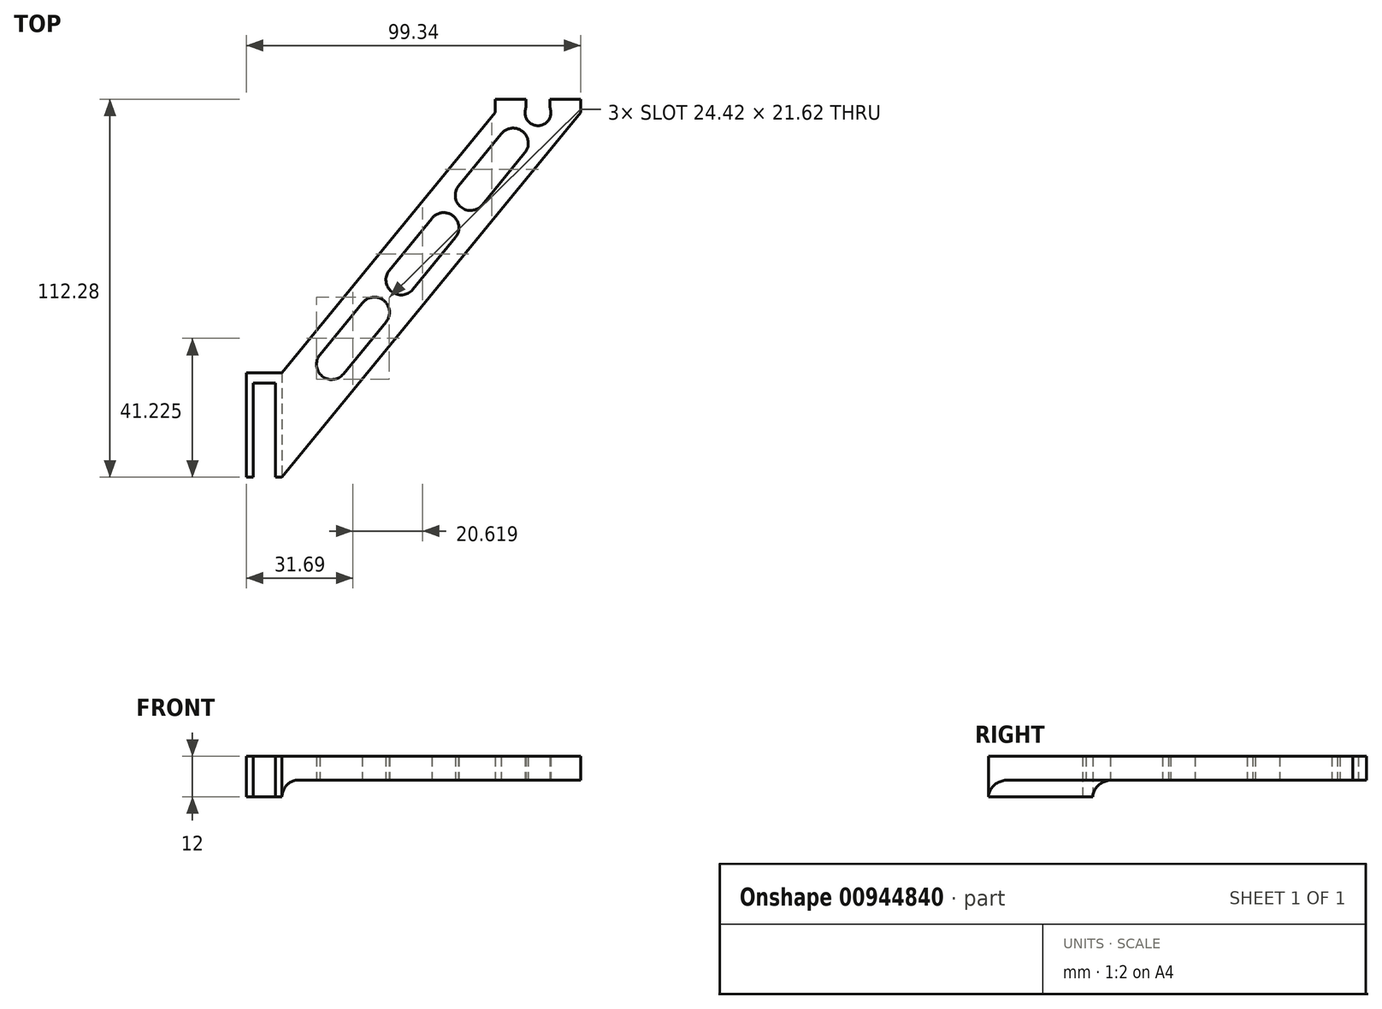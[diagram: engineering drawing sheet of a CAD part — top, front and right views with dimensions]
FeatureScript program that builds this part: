
annotation { "Feature Type Name" : "Feature", "Feature Type Description" : "" }
export const myFeature = defineFeature(function(context is Context, id is Id, definition is map)
    precondition{}
    {
        {
            var Q0;
            Q0=qCreatedBy(makeId("Top.planeOp"),FACE);
            var sketch = newSketch(context, id + "F0", { "sketchPlane" : qUnion([Q0])});
            skLineSegment(sketch, "E0", {"start": v(-54.43, -23.7) * mm, "end": v(-47.83, -23.7) * mm});
            skLineSegment(sketch, "E1", {"start": v(-47.83, -23.7) * mm, "end": v(-47.83, -51.7) * mm});
            skLineSegment(sketch, "E2", {"start": v(-54.43, -23.7) * mm, "end": v(-54.43, -51.7) * mm});
            skLineSegment(sketch, "E3", {"start": v(-54.43, -51.7) * mm, "end": v(-56.43, -51.7) * mm});
            skLineSegment(sketch, "E4", {"start": v(-56.43, -51.7) * mm, "end": v(-56.43, -20.7) * mm});
            skLineSegment(sketch, "E5", {"start": v(-56.43, -20.7) * mm, "end": v(-45.83, -20.7) * mm});
            skLineSegment(sketch, "E6", {"start": v(-45.83, -20.7) * mm, "end": v(17.5, 56.59) * mm});
            skLineSegment(sketch, "E7", {"start": v(-47.83, -51.7) * mm, "end": v(-45.83, -51.7) * mm});
            skLineSegment(sketch, "E8", {"start": v(-45.83, -51.7) * mm, "end": v(42.91, 56.59) * mm});
            skLineSegment(sketch, "E9", {"start": v(-45.83, -20.7) * mm, "end": v(-45.83, -51.7) * mm});
            skLineSegment(sketch, "E10", {"start": v(17.5, 56.59) * mm, "end": v(17.5, 60.59) * mm});
            skLineSegment(sketch, "E11", {"start": v(17.5, 60.59) * mm, "end": v(26.7, 60.59) * mm});
            skLineSegment(sketch, "E12", {"start": v(42.91, 60.59) * mm, "end": v(42.91, 56.59) * mm});
            skArc(sketch, "E13", {"start": v(26.7, 58.18) * mm, "mid": v(30.2, 52.74) * mm, "end": v(33.71, 58.18) * mm});
            skPoint(sketch, "E14", {"position": v(30.2, 60.59) * mm});
            skLineSegment(sketch, "E15", {"start": v(26.7, 60.59) * mm, "end": v(26.7, 58.18) * mm});
            skLineSegment(sketch, "E16", {"start": v(33.71, 60.59) * mm, "end": v(33.71, 58.18) * mm});
            skLineSegment(sketch, "E17.trimOffspring", {"start": v(33.71, 60.59) * mm, "end": v(42.91, 60.59) * mm});
            skLineSegment(sketch, "E18", {"start": v(-34.62, -15.41) * mm, "end": v(-21.94, 0.05) * mm});
            skLineSegment(sketch, "E19", {"start": v(-14.92, -5.58) * mm, "end": v(-27.6, -21.05) * mm});
            skArc(sketch, "E20", {"start": v(-14.92, -5.58) * mm, "mid": v(-15.59, 0.78) * mm, "end": v(-21.94, 0.05) * mm});
            skArc(sketch, "E21", {"start": v(-34.62, -15.41) * mm, "mid": v(-33.9, -21.7) * mm, "end": v(-27.6, -21.05) * mm});
            skLineSegment(sketch, "E22.1.0.0", {"start": v(-14, 9.7) * mm, "end": v(-1.32, 25.17) * mm});
            skLineSegment(sketch, "E22.1.0.1", {"start": v(5.7, 19.53) * mm, "end": v(-6.98, 4.07) * mm});
            skArc(sketch, "E22.1.0.2", {"start": v(5.7, 19.53) * mm, "mid": v(5.03, 25.9) * mm, "end": v(-1.32, 25.17) * mm});
            skArc(sketch, "E22.1.0.3", {"start": v(-14, 9.7) * mm, "mid": v(-13.28, 3.4) * mm, "end": v(-6.98, 4.07) * mm});
            skLineSegment(sketch, "E22.2.0.0", {"start": v(6.62, 34.81) * mm, "end": v(19.3, 50.28) * mm});
            skLineSegment(sketch, "E22.2.0.1", {"start": v(26.32, 44.65) * mm, "end": v(13.64, 29.18) * mm});
            skArc(sketch, "E22.2.0.2", {"start": v(26.32, 44.65) * mm, "mid": v(25.65, 51.01) * mm, "end": v(19.3, 50.28) * mm});
            skArc(sketch, "E22.2.0.3", {"start": v(6.62, 34.81) * mm, "mid": v(7.34, 28.52) * mm, "end": v(13.64, 29.18) * mm});
            skLineSegment(sketch, "E22.direction1", {"start": v(-34.62, -15.41) * mm, "end": v(-14, 9.7) * mm, "construction": true});
            skSolve(sketch);
        }
        {
            var Q0;
            Q0=makeQuery(id+"F0.imprint","IMPRINT",FACE,{"disambiguationData":[TD([[makeQuery(id+"F0.imprint","IMPRINT",EDGE,{"derivedFrom":sQuery(id+"F0.wireOp",EDGE,"E6")}),-1.0]])]});
            var Q1;
            Q1=makeQuery(id+"F0.imprint","IMPRINT",FACE,{"disambiguationData":[TD([[makeQuery(id+"F0.imprint","IMPRINT",EDGE,{"derivedFrom":sQuery(id+"F0.wireOp",EDGE,"E0")}),1.0]])]});
            extrude(context, id + "F1", {"entities" : qUnion([Q0, Q1]), "depth" : 12 * mm, "offsetDistance" : 25 * mm});
        }
        {
            var Q0;
            Q0=makeQuery(id+"F0.imprint","IMPRINT",FACE,{"disambiguationData":[TD([[makeQuery(id+"F0.imprint","IMPRINT",EDGE,{"derivedFrom":sQuery(id+"F0.wireOp",EDGE,"E18")}),-1.0]])]});
            var Q1;
            Q1=makeQuery(id+"F0.imprint","IMPRINT",FACE,{"disambiguationData":[TD([[makeQuery(id+"F0.imprint","IMPRINT",EDGE,{"derivedFrom":sQuery(id+"F0.wireOp",EDGE,"E22.1.0.0")}),-1.0]])]});
            var Q2;
            Q2=makeQuery(id+"F0.imprint","IMPRINT",FACE,{"disambiguationData":[TD([[makeQuery(id+"F0.imprint","IMPRINT",EDGE,{"derivedFrom":sQuery(id+"F0.wireOp",EDGE,"E22.2.0.0")}),-1.0]])]});
            extrude(context, id + "F2", {"entities" : qUnion([Q0, Q1, Q2]), "operationType" : NewBodyOperationType.REMOVE, "oppositeDirection" : true, "depth" : 25 * mm, "offsetDistance" : 25 * mm});
        }
        {
            var Q0;
            Q0=makeQuery(id+"F0.imprint","IMPRINT",FACE,{"disambiguationData":[TD([[makeQuery(id+"F0.imprint","IMPRINT",EDGE,{"derivedFrom":sQuery(id+"F0.wireOp",EDGE,"E6")}),-1.0]])]});
            extrude(context, id + "F3", {"entities" : qUnion([Q0]), "operationType" : NewBodyOperationType.REMOVE, "depth" : 5 * mm, "offsetDistance" : 25 * mm});
        }
        {
            var Q0;
            Q0=makeQuery(id+"F3.boolean.opBoolean","COPY",EDGE,{"derivedFrom":makeQuery(id+"F3.opExtrude","CAP_EDGE",EDGE,{"disambiguationData":[OSD([sQuery(id+"F0.wireOp",EDGE,"E9")])],"isStart":false})});
            fillet(context, id + "F4", {"entities" : qUnion([Q0]), "radius" : 5 * mm, "tangentPropagation" : true, "allowEdgeOverflow" : false});
        }
    });
